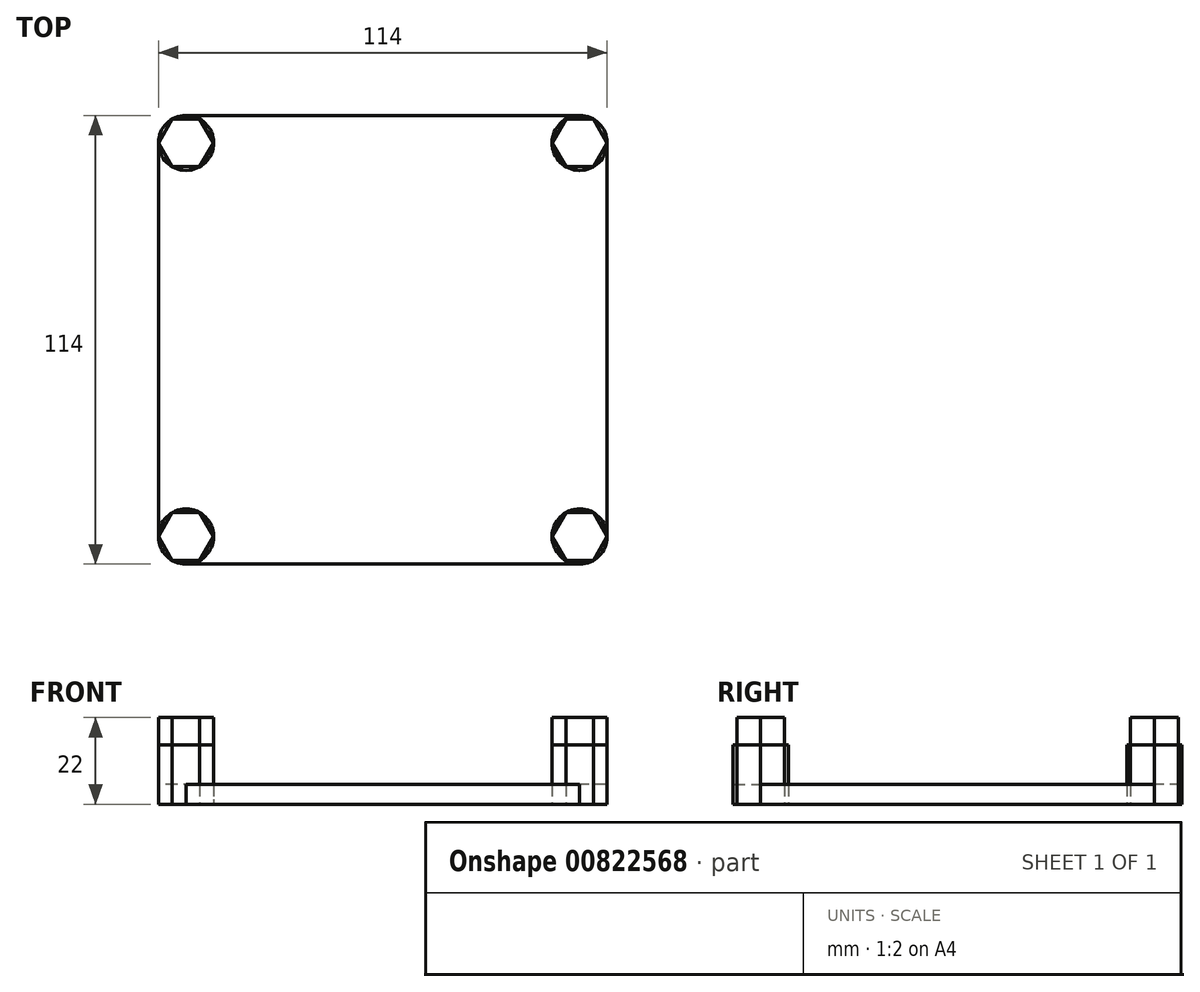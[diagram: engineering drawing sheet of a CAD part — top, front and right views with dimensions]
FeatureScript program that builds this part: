
annotation { "Feature Type Name" : "Feature", "Feature Type Description" : "" }
export const myFeature = defineFeature(function(context is Context, id is Id, definition is map)
    precondition{}
    {
        {
            var Q0;
            Q0=qCreatedBy(makeId("Top.planeOp"),FACE);
            var sketch = newSketch(context, id + "F0", { "sketchPlane" : qUnion([Q0])});
            skPoint(sketch, "E0", {"position": v(-52.94, 50) * mm});
            skPoint(sketch, "E1", {"position": v(47.06, 50) * mm});
            skPoint(sketch, "E2", {"position": v(47.06, -50) * mm});
            skCircle(sketch, "E3.cCircle", {"center": v(-52.94, 50) * mm, "radius": 7 * mm});
            skLineSegment(sketch, "E3.0", {"start": v(-45.94, 50) * mm, "end": v(-49.44, 43.94) * mm});
            skLineSegment(sketch, "E3.1", {"start": v(-49.44, 43.94) * mm, "end": v(-56.44, 43.94) * mm});
            skLineSegment(sketch, "E3.2", {"start": v(-56.44, 43.94) * mm, "end": v(-59.94, 50) * mm});
            skLineSegment(sketch, "E3.3", {"start": v(-59.94, 50) * mm, "end": v(-56.44, 56.06) * mm});
            skLineSegment(sketch, "E3.4", {"start": v(-56.44, 56.06) * mm, "end": v(-49.44, 56.06) * mm});
            skLineSegment(sketch, "E3.5", {"start": v(-49.44, 56.06) * mm, "end": v(-45.94, 50) * mm});
            skCircle(sketch, "E4.cCircle", {"center": v(47.06, 50) * mm, "radius": 7 * mm});
            skLineSegment(sketch, "E4.0", {"start": v(54.06, 50) * mm, "end": v(50.56, 43.94) * mm});
            skLineSegment(sketch, "E4.1", {"start": v(50.56, 43.94) * mm, "end": v(43.56, 43.94) * mm});
            skLineSegment(sketch, "E4.2", {"start": v(43.56, 43.94) * mm, "end": v(40.06, 50) * mm});
            skLineSegment(sketch, "E4.3", {"start": v(40.06, 50) * mm, "end": v(43.56, 56.06) * mm});
            skLineSegment(sketch, "E4.4", {"start": v(43.56, 56.06) * mm, "end": v(50.56, 56.06) * mm});
            skLineSegment(sketch, "E4.5", {"start": v(50.56, 56.06) * mm, "end": v(54.06, 50) * mm});
            skCircle(sketch, "E5.cCircle", {"center": v(47.06, -50) * mm, "radius": 7 * mm});
            skLineSegment(sketch, "E5.0", {"start": v(54.06, -50) * mm, "end": v(50.56, -56.06) * mm});
            skLineSegment(sketch, "E5.1", {"start": v(50.56, -56.06) * mm, "end": v(43.56, -56.06) * mm});
            skLineSegment(sketch, "E5.2", {"start": v(43.56, -56.06) * mm, "end": v(40.06, -50) * mm});
            skLineSegment(sketch, "E5.3", {"start": v(40.06, -50) * mm, "end": v(43.56, -43.94) * mm});
            skLineSegment(sketch, "E5.4", {"start": v(43.56, -43.94) * mm, "end": v(50.56, -43.94) * mm});
            skLineSegment(sketch, "E5.5", {"start": v(50.56, -43.94) * mm, "end": v(54.06, -50) * mm});
            skPoint(sketch, "E6", {"position": v(-52.94, -50) * mm});
            skCircle(sketch, "E7.cCircle", {"center": v(-52.94, -50) * mm, "radius": 7 * mm});
            skLineSegment(sketch, "E7.0", {"start": v(-45.94, -50) * mm, "end": v(-49.44, -56.06) * mm});
            skLineSegment(sketch, "E7.1", {"start": v(-49.44, -56.06) * mm, "end": v(-56.44, -56.06) * mm});
            skLineSegment(sketch, "E7.2", {"start": v(-56.44, -56.06) * mm, "end": v(-59.94, -50) * mm});
            skLineSegment(sketch, "E7.3", {"start": v(-59.94, -50) * mm, "end": v(-56.44, -43.94) * mm});
            skLineSegment(sketch, "E7.4", {"start": v(-56.44, -43.94) * mm, "end": v(-49.44, -43.94) * mm});
            skLineSegment(sketch, "E7.5", {"start": v(-49.44, -43.94) * mm, "end": v(-45.94, -50) * mm});
            skLineSegment(sketch, "E8", {"start": v(-52.94, -57) * mm, "end": v(47.06, -57) * mm});
            skLineSegment(sketch, "E9", {"start": v(54.06, -50) * mm, "end": v(54.06, 50) * mm});
            skLineSegment(sketch, "E10", {"start": v(47.06, 57) * mm, "end": v(-52.94, 57) * mm});
            skLineSegment(sketch, "E11", {"start": v(-59.94, 50) * mm, "end": v(-59.94, -50) * mm});
            skSolve(sketch);
        }
        {
            var Q0;
            {var subQ5=sQuery(id+"F0.wireOp",EDGE,"E8");Q0=makeQuery(id+"F0.imprint","IMPRINT",FACE,{"disambiguationData":[TD([[makeQuery(id+"F0.imprint","IMPRINT",EDGE,{"derivedFrom":subQ5}),1.0]])]});}
            extrude(context, id + "F1", {"entities" : qUnion([Q0]), "depth" : 5 * mm, "offsetDistance" : 25 * mm});
        }
        {
            var Q0;
            Q0=makeQuery(id+"F0.imprint","IMPRINT",FACE,{"disambiguationData":[TD([[makeQuery(id+"F0.imprint","IMPRINT",EDGE,{"derivedFrom":sQuery(id+"F0.wireOp",EDGE,"E3.0")}),-1.0]])]});
            var Q1;
            Q1=makeQuery(id+"F0.imprint","IMPRINT",FACE,{"disambiguationData":[TD([[makeQuery(id+"F0.imprint","IMPRINT",EDGE,{"derivedFrom":sQuery(id+"F0.wireOp",EDGE,"E5.0")}),-1.0]])]});
            var Q2;
            Q2=makeQuery(id+"F0.imprint","IMPRINT",FACE,{"disambiguationData":[TD([[makeQuery(id+"F0.imprint","IMPRINT",EDGE,{"derivedFrom":sQuery(id+"F0.wireOp",EDGE,"E7.0")}),-1.0]])]});
            var Q3;
            {var subQ0=sQuery(id+"F0.wireOp",EDGE,"E5.0");Q3=makeQuery(id+"F0.imprint","IMPRINT",FACE,{"disambiguationData":[TD([[makeQuery(id+"F0.imprint","IMPRINT",EDGE,{"derivedFrom":subQ0}),1.0]])]});}
            var Q4;
            {var subQ0=sQuery(id+"F0.wireOp",EDGE,"E5.4");Q4=makeQuery(id+"F0.imprint","IMPRINT",FACE,{"disambiguationData":[TD([[makeQuery(id+"F0.imprint","IMPRINT",EDGE,{"derivedFrom":subQ0}),1.0]])]});}
            var Q5;
            {var subQ0=sQuery(id+"F0.wireOp",EDGE,"E5.3");Q5=makeQuery(id+"F0.imprint","IMPRINT",FACE,{"disambiguationData":[TD([[makeQuery(id+"F0.imprint","IMPRINT",EDGE,{"derivedFrom":subQ0}),1.0]])]});}
            var Q6;
            {var subQ0=sQuery(id+"F0.wireOp",EDGE,"E5.2");Q6=makeQuery(id+"F0.imprint","IMPRINT",FACE,{"disambiguationData":[TD([[makeQuery(id+"F0.imprint","IMPRINT",EDGE,{"derivedFrom":subQ0}),1.0]])]});}
            var Q7;
            {var subQ0=sQuery(id+"F0.wireOp",EDGE,"E7.5");Q7=makeQuery(id+"F0.imprint","IMPRINT",FACE,{"disambiguationData":[TD([[makeQuery(id+"F0.imprint","IMPRINT",EDGE,{"derivedFrom":subQ0}),1.0]])]});}
            var Q8;
            {var subQ0=sQuery(id+"F0.wireOp",EDGE,"E7.4");Q8=makeQuery(id+"F0.imprint","IMPRINT",FACE,{"disambiguationData":[TD([[makeQuery(id+"F0.imprint","IMPRINT",EDGE,{"derivedFrom":subQ0}),1.0]])]});}
            var Q9;
            {var subQ0=sQuery(id+"F0.wireOp",EDGE,"E7.0");Q9=makeQuery(id+"F0.imprint","IMPRINT",FACE,{"disambiguationData":[TD([[makeQuery(id+"F0.imprint","IMPRINT",EDGE,{"derivedFrom":subQ0}),1.0]])]});}
            var Q10;
            {var subQ0=sQuery(id+"F0.wireOp",EDGE,"E7.3");Q10=makeQuery(id+"F0.imprint","IMPRINT",FACE,{"disambiguationData":[TD([[makeQuery(id+"F0.imprint","IMPRINT",EDGE,{"derivedFrom":subQ0}),1.0]])]});}
            var Q11;
            {var subQ0=sQuery(id+"F0.wireOp",EDGE,"E7.1");Q11=makeQuery(id+"F0.imprint","IMPRINT",FACE,{"disambiguationData":[TD([[makeQuery(id+"F0.imprint","IMPRINT",EDGE,{"derivedFrom":subQ0}),1.0]])]});}
            var Q12;
            {var subQ0=sQuery(id+"F0.wireOp",EDGE,"E7.2");Q12=makeQuery(id+"F0.imprint","IMPRINT",FACE,{"disambiguationData":[TD([[makeQuery(id+"F0.imprint","IMPRINT",EDGE,{"derivedFrom":subQ0}),1.0]])]});}
            var Q13;
            {var subQ0=sQuery(id+"F0.wireOp",EDGE,"E3.4");Q13=makeQuery(id+"F0.imprint","IMPRINT",FACE,{"disambiguationData":[TD([[makeQuery(id+"F0.imprint","IMPRINT",EDGE,{"derivedFrom":subQ0}),1.0]])]});}
            var Q14;
            {var subQ0=sQuery(id+"F0.wireOp",EDGE,"E3.5");Q14=makeQuery(id+"F0.imprint","IMPRINT",FACE,{"disambiguationData":[TD([[makeQuery(id+"F0.imprint","IMPRINT",EDGE,{"derivedFrom":subQ0}),1.0]])]});}
            var Q15;
            {var subQ0=sQuery(id+"F0.wireOp",EDGE,"E3.0");Q15=makeQuery(id+"F0.imprint","IMPRINT",FACE,{"disambiguationData":[TD([[makeQuery(id+"F0.imprint","IMPRINT",EDGE,{"derivedFrom":subQ0}),1.0]])]});}
            var Q16;
            {var subQ0=sQuery(id+"F0.wireOp",EDGE,"E3.3");Q16=makeQuery(id+"F0.imprint","IMPRINT",FACE,{"disambiguationData":[TD([[makeQuery(id+"F0.imprint","IMPRINT",EDGE,{"derivedFrom":subQ0}),1.0]])]});}
            var Q17;
            {var subQ0=sQuery(id+"F0.wireOp",EDGE,"E3.2");Q17=makeQuery(id+"F0.imprint","IMPRINT",FACE,{"disambiguationData":[TD([[makeQuery(id+"F0.imprint","IMPRINT",EDGE,{"derivedFrom":subQ0}),1.0]])]});}
            var Q18;
            {var subQ0=sQuery(id+"F0.wireOp",EDGE,"E3.1");Q18=makeQuery(id+"F0.imprint","IMPRINT",FACE,{"disambiguationData":[TD([[makeQuery(id+"F0.imprint","IMPRINT",EDGE,{"derivedFrom":subQ0}),1.0]])]});}
            var Q19;
            {var subQ0=sQuery(id+"F0.wireOp",EDGE,"E4.4");Q19=makeQuery(id+"F0.imprint","IMPRINT",FACE,{"disambiguationData":[TD([[makeQuery(id+"F0.imprint","IMPRINT",EDGE,{"derivedFrom":subQ0}),1.0]])]});}
            var Q20;
            {var subQ0=sQuery(id+"F0.wireOp",EDGE,"E4.5");Q20=makeQuery(id+"F0.imprint","IMPRINT",FACE,{"disambiguationData":[TD([[makeQuery(id+"F0.imprint","IMPRINT",EDGE,{"derivedFrom":subQ0}),1.0]])]});}
            var Q21;
            {var subQ0=sQuery(id+"F0.wireOp",EDGE,"E4.0");Q21=makeQuery(id+"F0.imprint","IMPRINT",FACE,{"disambiguationData":[TD([[makeQuery(id+"F0.imprint","IMPRINT",EDGE,{"derivedFrom":subQ0}),1.0]])]});}
            var Q22;
            {var subQ0=sQuery(id+"F0.wireOp",EDGE,"E4.1");Q22=makeQuery(id+"F0.imprint","IMPRINT",FACE,{"disambiguationData":[TD([[makeQuery(id+"F0.imprint","IMPRINT",EDGE,{"derivedFrom":subQ0}),1.0]])]});}
            var Q23;
            {var subQ0=sQuery(id+"F0.wireOp",EDGE,"E4.2");Q23=makeQuery(id+"F0.imprint","IMPRINT",FACE,{"disambiguationData":[TD([[makeQuery(id+"F0.imprint","IMPRINT",EDGE,{"derivedFrom":subQ0}),1.0]])]});}
            var Q24;
            {var subQ0=sQuery(id+"F0.wireOp",EDGE,"E4.3");Q24=makeQuery(id+"F0.imprint","IMPRINT",FACE,{"disambiguationData":[TD([[makeQuery(id+"F0.imprint","IMPRINT",EDGE,{"derivedFrom":subQ0}),1.0]])]});}
            var Q25;
            Q25=makeQuery(id+"F0.imprint","IMPRINT",FACE,{"disambiguationData":[TD([[makeQuery(id+"F0.imprint","IMPRINT",EDGE,{"derivedFrom":sQuery(id+"F0.wireOp",EDGE,"E4.0")}),-1.0]])]});
            var Q26;
            {var subQ0=sQuery(id+"F0.wireOp",EDGE,"E5.1");Q26=makeQuery(id+"F0.imprint","IMPRINT",FACE,{"disambiguationData":[TD([[makeQuery(id+"F0.imprint","IMPRINT",EDGE,{"derivedFrom":subQ0}),1.0]])]});}
            var Q27;
            {var subQ0=sQuery(id+"F0.wireOp",EDGE,"E5.5");Q27=makeQuery(id+"F0.imprint","IMPRINT",FACE,{"disambiguationData":[TD([[makeQuery(id+"F0.imprint","IMPRINT",EDGE,{"derivedFrom":subQ0}),1.0]])]});}
            extrude(context, id + "F2", {"entities" : qUnion([Q0, Q1, Q2, Q3, Q4, Q5, Q6, Q7, Q8, Q9, Q10, Q11, Q12, Q13, Q14, Q15, Q16, Q17, Q18, Q19, Q20, Q21, Q22, Q23, Q24, Q25, Q26, Q27]), "depth" : 15 * mm, "offsetDistance" : 25 * mm});
        }
        {
            var Q0;
            Q0=makeQuery(id+"F0.imprint","IMPRINT",FACE,{"disambiguationData":[TD([[makeQuery(id+"F0.imprint","IMPRINT",EDGE,{"derivedFrom":sQuery(id+"F0.wireOp",EDGE,"E3.0")}),-1.0]])]});
            var Q1;
            Q1=makeQuery(id+"F0.imprint","IMPRINT",FACE,{"disambiguationData":[TD([[makeQuery(id+"F0.imprint","IMPRINT",EDGE,{"derivedFrom":sQuery(id+"F0.wireOp",EDGE,"E5.0")}),-1.0]])]});
            var Q2;
            Q2=makeQuery(id+"F0.imprint","IMPRINT",FACE,{"disambiguationData":[TD([[makeQuery(id+"F0.imprint","IMPRINT",EDGE,{"derivedFrom":sQuery(id+"F0.wireOp",EDGE,"E7.0")}),-1.0]])]});
            var Q3;
            Q3=makeQuery(id+"F0.imprint","IMPRINT",FACE,{"disambiguationData":[TD([[makeQuery(id+"F0.imprint","IMPRINT",EDGE,{"derivedFrom":sQuery(id+"F0.wireOp",EDGE,"E4.0")}),-1.0]])]});
            extrude(context, id + "F3", {"entities" : qUnion([Q0, Q1, Q2, Q3]), "depth" : 22 * mm, "offsetDistance" : 25 * mm});
        }
    });
